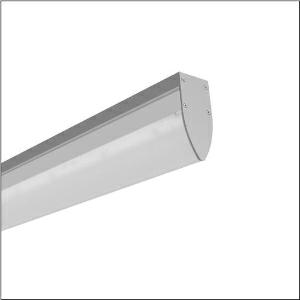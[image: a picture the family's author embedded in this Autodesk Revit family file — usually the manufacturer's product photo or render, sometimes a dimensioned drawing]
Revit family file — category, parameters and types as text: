
# Revit family: mira_r__21_td_51fr527k444a_1922
name_source: partatom
category: Lighting Fixtures
units: mm (PartAtom-declared; Revit-internal decimal feet)

## family parameters
Cut with Voids When Loaded = No
Host = Face
Light Source = No
Part Type = Normal
Room Calculation Point = No
Round Connector Dimension = Use Diameter
Shared = No

## types (1)
- Mira® 21 TD (1 x LED, 4030 lm, 27 W, 4000K)
    Apparent Load = 27 VA
    CIE Flux Codes = 40 68 87 81 100
    Color Rendering = 80
    Color Temperature = 4000K
    Default Elevation = 1800 mm
    Description = Mira® 21 TD, clean room luminaire, primary light control with reflector, primary optical cover: cover, of PMMA, frosted, light emission: direct distribution, primary light characteristic: symmetric, installation type: surface-mounted, LED, rated luminous flux: 4.030lm, luminous efficacy: 149lm/W, light colour: 840, colour temperature: 4000K, control gear: ECG, with terminal, 3-pole, max. 2.5mm², mains connection: 230V, AC, 50/60Hz, rated input power: 27W, luminaire housing, of sheet steel, coated, pure white (RAL 9010), length: 1.200mm, width: 55mm, height: 120mm, protection rating (complete): IP43, insulation class (complete): insulation class I (protective earthing), certification: CE, UKCA, permissible operating ambient temperature: -5..+40°C, standard: EN 50419, packaging unit: 1 piece
    Height = 0 mm  [stored 0 ft]
    Lamp = 1 x LED
    Lamp Light Flux = 4030 lm
    Lamp Power = 27 W
    Lamp count = 1
    Length = 1200 mm
    Luminous efficacy = 149 lm/W
    Manufacturer = Siteco
    ModVariant = No
    Model = 51FR527K444A
    Mounting Place = Ceiling
    Mounting Type = Recessed
    Number of Poles = 1
    OnlyDefault = Yes
    Power Factor = 1
    Product Name = Mira® 21 TD
    Product group = clean room luminaire
    ProductGroupID = 402
    Protection Class = Protection class I
    Protection Degree = IP 43
    RLX_Detail_Level = 1
    RLX_Emergency_Light_Flux = 0 lm
    RLX_Emergency_Type = 0
    RLX_Emergency_Type_DB = No
    RlxData = <blob elided: 25141 chars, md5=7acb4c72>
    Socket = socket
    Standby Power = 0 W
    System Light Flux = 4030 lm
    System Power = 27 W
    Type Comments = Product without accessories
    Type Image = l_1007115.jpg
    URL = http://relux.com
    VarID = ---
    Voltage = 0 V
    Weight = 0.00 kg
    Width = 55 mm

note: [stored X ft] marks values corroborated as IEEE doubles in the binary element streams (Revit-internal decimal feet)

## geometry (parser evidence)
native form markers: Blend x4, Sweep x12
no freeform markers — native parametric forms only
